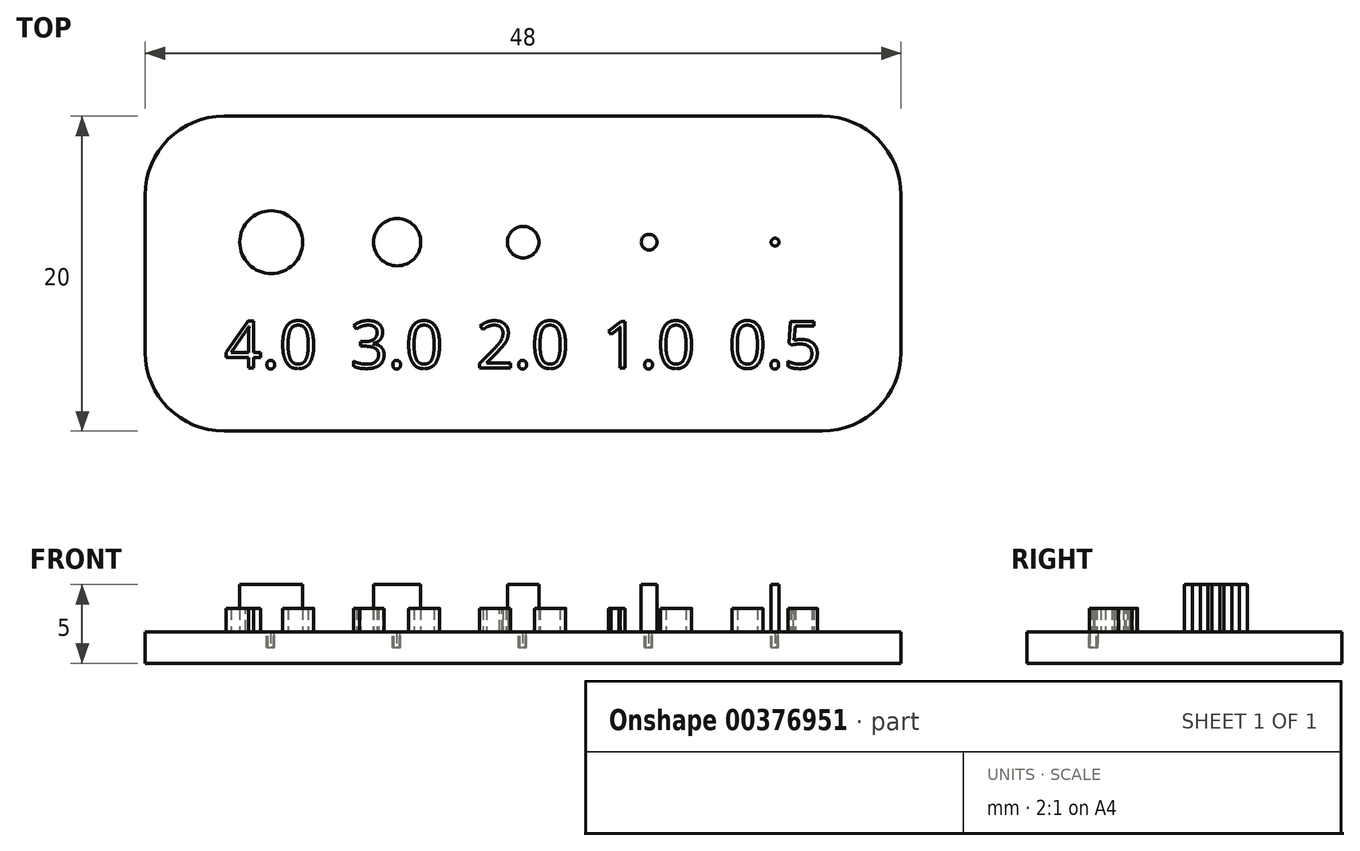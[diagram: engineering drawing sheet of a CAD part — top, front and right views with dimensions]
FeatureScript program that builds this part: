
annotation { "Feature Type Name" : "Feature", "Feature Type Description" : "" }
export const myFeature = defineFeature(function(context is Context, id is Id, definition is map)
    precondition{}
    {
        {
            var Q0;
            Q0=qCreatedBy(makeId("Top.planeOp"),FACE);
            var sketch = newSketch(context, id + "F0", { "sketchPlane" : qUnion([Q0])});
            skLineSegment(sketch, "E0.bottom", {"start": v(-32, 20) * mm, "end": v(16, 20) * mm});
            skLineSegment(sketch, "E0.top", {"start": v(-32, 0) * mm, "end": v(16, 0) * mm});
            skLineSegment(sketch, "E0.left", {"start": v(-32, 20) * mm, "end": v(-32, 0) * mm});
            skLineSegment(sketch, "E0.right", {"start": v(16, 20) * mm, "end": v(16, 0) * mm});
            skLineSegment(sketch, "E1", {"start": v(-32, 12) * mm, "end": v(13.46, 12) * mm, "construction": true});
            skCircle(sketch, "E2", {"center": v(-24, 12) * mm, "radius": 2 * mm});
            skCircle(sketch, "E3", {"center": v(-16, 12) * mm, "radius": 1.5 * mm});
            skCircle(sketch, "E4", {"center": v(-8, 12) * mm, "radius": 1 * mm});
            skCircle(sketch, "E5", {"center": v(0, 12) * mm, "radius": 0.5 * mm});
            skCircle(sketch, "E6", {"center": v(8, 12) * mm, "radius": 0.25 * mm});
            skText(sketch, "E7", { "text": "4.0", "fontName": "OpenSans-Regular.ttf"});
            skText(sketch, "E8", { "text": "3.0", "fontName": "OpenSans-Regular.ttf"});
            skText(sketch, "E9", { "text": "2.0", "fontName": "OpenSans-Regular.ttf"});
            skText(sketch, "E10", { "text": "1.0", "fontName": "OpenSans-Regular.ttf"});
            skText(sketch, "E11", { "text": "0.5", "fontName": "OpenSans-Regular.ttf"});
            const initialGuessF0  = {"E7": [-0.02697, 0.004, 1, 0, 0.003], "E8": [-0.01897, 0.004, 1, 0, 0.003], "E9": [-0.01097, 0.004, 1, 0, 0.003], "E10": [-0.00297, 0.004, 1, 0, 0.003], "E11": [0.00505, 0.004, 1, 0, 0.003]};
            skSetInitialGuess(sketch, initialGuessF0);
            skSolve(sketch);
        }
        {
            var Q0;
            Q0=makeQuery(id+"F0.imprint","IMPRINT",FACE,{"disambiguationData":[TD([[makeQuery(id+"F0.imprint","IMPRINT",EDGE,{"derivedFrom":sQuery(id+"F0.wireOp",EDGE,"E0.bottom")}),-1.0]])]});
            var sketch = newSketch(context, id + "F1", { "sketchPlane" : qUnion([Q0])});
            skLineSegment(sketch, "E12.0", {"start": v(-32, 0) * mm, "end": v(16, 0) * mm});
            skLineSegment(sketch, "E13.0", {"start": v(16, 20) * mm, "end": v(16, 0) * mm});
            skLineSegment(sketch, "E14.0", {"start": v(-32, 20) * mm, "end": v(16, 20) * mm});
            skLineSegment(sketch, "E15.0", {"start": v(-32, 20) * mm, "end": v(-32, 0) * mm});
            skSolve(sketch);
        }
        {
            var Q0;
            Q0=qSketchRegion(id+"F1",true);
            extrude(context, id + "F2", {"entities" : qUnion([Q0]), "oppositeDirection" : true, "depth" : 2 * mm});
        }
        {
            var Q0;
            Q0=makeQuery(id+"F0.imprint","IMPRINT",FACE,{"disambiguationData":[TD([[makeQuery(id+"F0.imprint","IMPRINT",EDGE,{"derivedFrom":sQuery(id+"F0.wireOp",EDGE,"E2")}),1.0]])]});
            var Q1;
            Q1=makeQuery(id+"F0.imprint","IMPRINT",FACE,{"disambiguationData":[TD([[makeQuery(id+"F0.imprint","IMPRINT",EDGE,{"derivedFrom":sQuery(id+"F0.wireOp",EDGE,"E3")}),1.0]])]});
            var Q2;
            Q2=makeQuery(id+"F0.imprint","IMPRINT",FACE,{"disambiguationData":[TD([[makeQuery(id+"F0.imprint","IMPRINT",EDGE,{"derivedFrom":sQuery(id+"F0.wireOp",EDGE,"E4")}),1.0]])]});
            var Q3;
            Q3=makeQuery(id+"F0.imprint","IMPRINT",FACE,{"disambiguationData":[TD([[makeQuery(id+"F0.imprint","IMPRINT",EDGE,{"derivedFrom":sQuery(id+"F0.wireOp",EDGE,"E5")}),1.0]])]});
            var Q4;
            Q4=makeQuery(id+"F0.imprint","IMPRINT",FACE,{"disambiguationData":[TD([[makeQuery(id+"F0.imprint","IMPRINT",EDGE,{"derivedFrom":sQuery(id+"F0.wireOp",EDGE,"E6")}),1.0]])]});
            extrude(context, id + "F3", {"entities" : qUnion([Q0, Q1, Q2, Q3, Q4]), "operationType" : NewBodyOperationType.ADD, "depth" : 3 * mm});
        }
        {
            var Q0;
            Q0=makeQuery(id+"F0.imprint","IMPRINT",FACE,{"disambiguationData":[TD([[makeQuery(id+"F0.imprint","IMPRINT",EDGE,{"derivedFrom":sQuery(id+"F0.wireOp",EDGE,"E7.sketch_text.stroke-0")}),-1.0]])]});
            var Q1;
            Q1=makeQuery(id+"F0.imprint","IMPRINT",FACE,{"disambiguationData":[TD([[makeQuery(id+"F0.imprint","IMPRINT",EDGE,{"derivedFrom":sQuery(id+"F0.wireOp",EDGE,"E7.sketch_text.stroke-25")}),-1.0]])]});
            var Q2;
            Q2=makeQuery(id+"F0.imprint","IMPRINT",FACE,{"disambiguationData":[TD([[makeQuery(id+"F0.imprint","IMPRINT",EDGE,{"derivedFrom":sQuery(id+"F0.wireOp",EDGE,"E8.sketch_text.stroke-0")}),-1.0]])]});
            var Q3;
            Q3=makeQuery(id+"F0.imprint","IMPRINT",FACE,{"disambiguationData":[TD([[makeQuery(id+"F0.imprint","IMPRINT",EDGE,{"derivedFrom":sQuery(id+"F0.wireOp",EDGE,"E8.sketch_text.stroke-36")}),-1.0]])]});
            var Q4;
            Q4=makeQuery(id+"F0.imprint","IMPRINT",FACE,{"disambiguationData":[TD([[makeQuery(id+"F0.imprint","IMPRINT",EDGE,{"derivedFrom":sQuery(id+"F0.wireOp",EDGE,"E9.sketch_text.stroke-0")}),-1.0]])]});
            var Q5;
            Q5=makeQuery(id+"F0.imprint","IMPRINT",FACE,{"disambiguationData":[TD([[makeQuery(id+"F0.imprint","IMPRINT",EDGE,{"derivedFrom":sQuery(id+"F0.wireOp",EDGE,"E9.sketch_text.stroke-28")}),-1.0]])]});
            var Q6;
            Q6=makeQuery(id+"F0.imprint","IMPRINT",FACE,{"disambiguationData":[TD([[makeQuery(id+"F0.imprint","IMPRINT",EDGE,{"derivedFrom":sQuery(id+"F0.wireOp",EDGE,"E10.sketch_text.stroke-0")}),-1.0]])]});
            var Q7;
            Q7=makeQuery(id+"F0.imprint","IMPRINT",FACE,{"disambiguationData":[TD([[makeQuery(id+"F0.imprint","IMPRINT",EDGE,{"derivedFrom":sQuery(id+"F0.wireOp",EDGE,"E10.sketch_text.stroke-17")}),-1.0]])]});
            var Q8;
            Q8=makeQuery(id+"F0.imprint","IMPRINT",FACE,{"disambiguationData":[TD([[makeQuery(id+"F0.imprint","IMPRINT",EDGE,{"derivedFrom":sQuery(id+"F0.wireOp",EDGE,"E11.sketch_text.stroke-0")}),-1.0]])]});
            var Q9;
            Q9=makeQuery(id+"F0.imprint","IMPRINT",FACE,{"disambiguationData":[TD([[makeQuery(id+"F0.imprint","IMPRINT",EDGE,{"derivedFrom":sQuery(id+"F0.wireOp",EDGE,"E11.sketch_text.stroke-24")}),-1.0]])]});
            extrude(context, id + "F4", {"entities" : qUnion([Q0, Q1, Q2, Q3, Q4, Q5, Q6, Q7, Q8, Q9]), "operationType" : NewBodyOperationType.ADD, "depth" : 1.5 * mm});
        }
        {
            var Q0;
            Q0=makeQuery(id+"F0.imprint","IMPRINT",FACE,{"disambiguationData":[TD([[makeQuery(id+"F0.imprint","IMPRINT",EDGE,{"derivedFrom":sQuery(id+"F0.wireOp",EDGE,"E7.sketch_text.stroke-17")}),-1.0]])]});
            var Q1;
            Q1=makeQuery(id+"F0.imprint","IMPRINT",FACE,{"disambiguationData":[TD([[makeQuery(id+"F0.imprint","IMPRINT",EDGE,{"derivedFrom":sQuery(id+"F0.wireOp",EDGE,"E8.sketch_text.stroke-28")}),-1.0]])]});
            var Q2;
            Q2=makeQuery(id+"F0.imprint","IMPRINT",FACE,{"disambiguationData":[TD([[makeQuery(id+"F0.imprint","IMPRINT",EDGE,{"derivedFrom":sQuery(id+"F0.wireOp",EDGE,"E9.sketch_text.stroke-20")}),-1.0]])]});
            var Q3;
            Q3=makeQuery(id+"F0.imprint","IMPRINT",FACE,{"disambiguationData":[TD([[makeQuery(id+"F0.imprint","IMPRINT",EDGE,{"derivedFrom":sQuery(id+"F0.wireOp",EDGE,"E10.sketch_text.stroke-9")}),-1.0]])]});
            var Q4;
            Q4=makeQuery(id+"F0.imprint","IMPRINT",FACE,{"disambiguationData":[TD([[makeQuery(id+"F0.imprint","IMPRINT",EDGE,{"derivedFrom":sQuery(id+"F0.wireOp",EDGE,"E11.sketch_text.stroke-16")}),-1.0]])]});
            extrude(context, id + "F5", {"entities" : qUnion([Q0, Q1, Q2, Q3, Q4]), "operationType" : NewBodyOperationType.REMOVE, "oppositeDirection" : true, "depth" : 1 * mm});
        }
        {
            var Q0;
            Q0=makeQuery(id+"F2.opExtrude","SWEPT_EDGE",EDGE,{"disambiguationData":[OSD([sQuery(id+"F1.wireOp",EDGE,"E12.0"),sQuery(id+"F1.wireOp",EDGE,"E13.0")])]});
            var Q1;
            Q1=makeQuery(id+"F2.opExtrude","SWEPT_EDGE",EDGE,{"disambiguationData":[OSD([sQuery(id+"F1.wireOp",EDGE,"E13.0"),sQuery(id+"F1.wireOp",EDGE,"E14.0")])]});
            var Q2;
            Q2=makeQuery(id+"F2.opExtrude","SWEPT_EDGE",EDGE,{"disambiguationData":[OSD([sQuery(id+"F1.wireOp",EDGE,"E12.0"),sQuery(id+"F1.wireOp",EDGE,"E15.0")])]});
            var Q3;
            Q3=makeQuery(id+"F2.opExtrude","SWEPT_EDGE",EDGE,{"disambiguationData":[OSD([sQuery(id+"F1.wireOp",EDGE,"E14.0"),sQuery(id+"F1.wireOp",EDGE,"E15.0")])]});
            fillet(context, id + "F6", {"entities" : qUnion([Q0, Q1, Q2, Q3]), "radius" : 5 * mm, "tangentPropagation" : true, "allowEdgeOverflow" : false});
        }
    });
